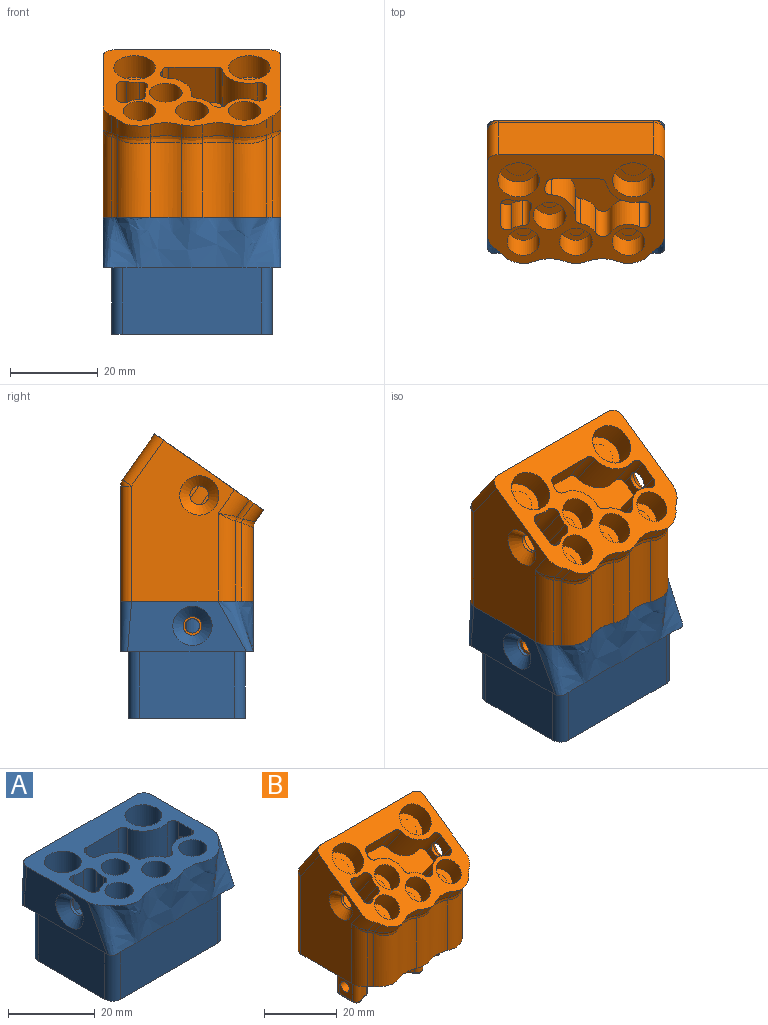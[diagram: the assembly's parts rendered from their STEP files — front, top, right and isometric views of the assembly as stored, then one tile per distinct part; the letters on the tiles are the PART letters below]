
ASSEMBLY  parts=2 mates=1
PART A: 55 faces, bbox 41.1x30.9x27.2 mm
  f0: cylinder r=1.6mm len=10mm, axis (0,0,1), area 29.4mm2, adj f1,f28,f29,f37,f47
  f1: plane 41.15x30.86mm, normal (0,0,1), area 665mm2, adj f0,f3,f4,f5,f6,f7,f8,f9
  f2: plane 40.88x30.59mm, normal (0,0,-1), area 253.7mm2, adj f3,f4,f5,f6,f7,f8,f38,f39
  f3: bspline ~40.6x11.6mm, area 535.9mm2, adj f1,f2,f4,f8
  f4: plane 27.1x11.6mm, normal (1,0,0), area 208.7mm2, adj f1,f2,f3,f5,f48
  f5: bspline ~39.24x28.84mm, area 37.4mm2, adj f1,f2,f4,f6
  f6: plane 37.4x11.6mm, normal (0,1,0), area 423.4mm2, adj f1,f2,f5,f7
  f7: bspline ~39.24x28.84mm, area 37.4mm2, adj f1,f2,f6,f8
  f8: plane 27.1x11.6mm, normal (-1,0,0), area 208.7mm2, adj f1,f2,f3,f7,f50
  f9: cylinder r=4.25mm len=26.7mm, axis (0,0,1), area 713mm2, adj f1,f46
  f10: cylinder r=3.25mm len=26.7mm, axis (0,0,1), area 545.2mm2, adj f1,f46
  f11: cylinder r=3.25mm len=26.7mm, axis (0,0,1), area 545.2mm2, adj f1,f46
  f12: cylinder r=4.25mm len=26.7mm, axis (0,0,1), area 713mm2, adj f1,f46
  f13: cylinder r=3.25mm len=26.7mm, axis (0,0,1), area 545.2mm2, adj f1,f46
  f14: cylinder r=3.25mm len=26.7mm, axis (0,0,1), area 545.2mm2, adj f1,f46
  f15: cylinder r=1.6mm len=10mm, axis (0,0,1), area 30.6mm2, adj f1,f16,f22,f23
  f16: plane 10x5.32mm, normal (1,0,0), area 38.7mm2, adj f1,f15,f17,f23,f49
  f17: cylinder r=1.6mm len=10mm, axis (0,0,1), area 35.3mm2, adj f1,f16,f18,f23
  f18: cylinder r=4.45mm len=10mm, axis (0,0,1), area 27mm2, adj f1,f17,f19,f23
  f19: cylinder r=1.6mm len=10mm, axis (0,0,1), area 27.7mm2, adj f1,f18,f20,f23
  f20: cylinder r=4.7mm len=10mm, axis (0,0,1), area 29.3mm2, adj f1,f19,f21,f23
  f21: cylinder r=1.6mm len=10mm, axis (0,0,1), area 35mm2, adj f1,f20,f22,f23
  f22: cylinder r=5.85mm len=10mm, axis (0,0,1), area 30.9mm2, adj f1,f15,f21,f23
  f23: plane 8.52x7.08mm, normal (0,0,1), area 49.5mm2, adj f15,f16,f17,f18,f19,f20,f21,f22
  f24: cylinder r=5.15mm len=10mm, axis (0,0,1), area 45.1mm2, adj f1,f25,f36,f37
  f25: cylinder r=1.85mm len=10mm, axis (0,0,1), area 39.4mm2, adj f1,f24,f26,f37
  f26: cylinder r=4.85mm len=10mm, axis (0,0,1), area 78.1mm2, adj f1,f25,f27,f37
  f27: cylinder r=1.6mm len=10mm, axis (0,0,1), area 34mm2, adj f1,f26,f28,f37
  f28: plane 10x4.21mm, normal (-1,0,0), area 28.1mm2, adj f0,f1,f27,f37,f47
  f29: cylinder r=6.25mm len=10mm, axis (0,0,1), area 106mm2, adj f0,f1,f30,f37
  f30: cylinder r=1.6mm len=10mm, axis (0,0,1), area 22.4mm2, adj f1,f29,f31,f37
  f31: plane 10.63x10mm, normal (0,-1,0), area 106.3mm2, adj f1,f30,f32,f37
  f32: cylinder r=1.6mm len=10mm, axis (0,0,1), area 22.4mm2, adj f1,f31,f33,f37
  f33: cylinder r=6.35mm len=10mm, axis (0,0,1), area 10.1mm2, adj f1,f32,f34,f37
  f34: cylinder r=1.6mm len=10mm, axis (0,0,1), area 29.5mm2, adj f1,f33,f35,f37
  f35: cylinder r=5.8mm len=10mm, axis (0,0,1), area 92.7mm2, adj f1,f34,f36,f37
  f36: cylinder r=1.6mm len=10mm, axis (0,0,1), area 23.2mm2, adj f1,f24,f35,f37
  f37: plane 24.18x16mm, normal (0,0,1), area 212.6mm2, adj f0,f24,f25,f26,f27,f28,f29,f30
  f38: plane 21.6x15.1mm, normal (1,0,0), area 317.6mm2, adj f2,f39,f45,f46,f54
  f39: cylinder r=2.5mm len=15.1mm, axis (0,0,1), area 59.3mm2, adj f2,f38,f40,f46
  f40: plane 31.6x15.1mm, normal (0,-1,0), area 477.2mm2, adj f2,f39,f41,f46
  f41: cylinder r=2.5mm len=15.1mm, axis (0,0,1), area 59.3mm2, adj f2,f40,f42,f46
  f42: plane 21.6x15.1mm, normal (-1,0,0), area 326.2mm2, adj f2,f41,f43,f46
  f43: cylinder r=2.5mm len=15.1mm, axis (0,0,1), area 59.3mm2, adj f2,f42,f44,f46
  f44: plane 31.6x15.1mm, normal (0,1,0), area 468.6mm2, adj f2,f43,f45,f46,f52
  f45: cylinder r=2.5mm len=15.1mm, axis (0,0,1), area 59.3mm2, adj f2,f38,f44,f46
  f46: plane 36.6x26.6mm, normal (0,0,-1), area 722mm2, adj f9,f10,f11,f12,f13,f14,f38,f39
  f47: cylinder r=2.15mm len=4.3mm, axis (1,0,0), area 13.1mm2, adj f0,f28,f48
  f48: cone r=2.15mm half-angle=45deg, axis (1,0,0), area 68.6mm2, adj f4,f47
  f49: cylinder r=2.15mm len=4.3mm, axis (-1,0,0), area 10.4mm2, adj f16,f50
  f50: cone r=2.15mm half-angle=45deg, axis (-1,0,0), area 68.6mm2, adj f8,f49
  f51: cone r=0mm half-angle=59deg, axis (0,1,0), area 10mm2, adj f52
  f52: cylinder r=1.65mm len=12.85mm, axis (0,1,0), area 133.2mm2, adj f44,f51
  f53: cone r=0mm half-angle=59deg, axis (1,0,0), area 10mm2, adj f54
  f54: cylinder r=1.65mm len=12.85mm, axis (1,0,0), area 133.2mm2, adj f38,f53
PART B: 167 faces, bbox 41.5x33.5x48.6 mm
  f0: torus R=0.85mm, axis (0,0,1), area 1.5mm2, adj f1,f164,f165,f166
  f1: cylinder r=1.45mm len=9mm, axis (0,0,1), area 25mm2, adj f0,f2,f162,f163
  f2: plane 40.6x30.3mm, normal (0,0,-1), area 534.2mm2, adj f1,f3,f8,f14,f20,f25,f31,f36
  f3: cylinder r=4mm len=8mm, axis (0,0,-1), area 175.9mm2, adj f2,f4
  f4: plane 8x8mm, normal (0,0,-1), area 37.7mm2, adj f3,f5
  f5: cylinder r=2mm len=15.32mm, axis (0,0,1), area 184.6mm2, adj f4,f6
  f6: cylinder r=2mm len=4.78mm, axis (0,-0.57,0.82), area 25mm2, adj f5,f7
  f7: plane 4x3.28mm, normal (0,0.57,-0.82), area 12.6mm2, adj f6
  f8: cylinder r=4mm len=8mm, axis (0,0,-1), area 175.9mm2, adj f2,f9
  f9: plane 8x8mm, normal (0,0,-1), area 37.7mm2, adj f8,f10
  f10: cylinder r=2mm len=12.7mm, axis (0,0,1), area 149.9mm2, adj f9,f11,f12,f13
  f11: cylinder r=2mm len=3.54mm, axis (0,-0.57,0.82), area 0mm2, adj f10,f13
  f12: cylinder r=2.55mm len=1.79mm, axis (0,-0.57,0.82), area 0mm2, adj f10,f13
  f13: plane 4.88x4.61mm, normal (0,0.57,-0.82), area 14.6mm2, adj f10,f11,f12
  f14: cylinder r=4mm len=8mm, axis (0,0,-1), area 175.9mm2, adj f2,f15
  f15: plane 8x8mm, normal (0,0,-1), area 37.7mm2, adj f14,f16
  f16: cylinder r=2mm len=12.7mm, axis (0,0,1), area 149.9mm2, adj f15,f17,f18,f19
  f17: cylinder r=2mm len=3.54mm, axis (0,-0.57,0.82), area 0mm2, adj f16,f19
  f18: cylinder r=2.55mm len=1.79mm, axis (0,-0.57,0.82), area 0mm2, adj f16,f19
  f19: plane 4.88x4.61mm, normal (0,0.57,-0.82), area 14.6mm2, adj f16,f17,f18
  f20: cylinder r=5.5mm len=11mm, axis (0,0,-1), area 241.9mm2, adj f2,f21
  f21: plane 11x11mm, normal (0,0,-1), area 66.8mm2, adj f20,f22
  f22: cylinder r=3mm len=18.78mm, axis (0,0,1), area 336.1mm2, adj f21,f23
  f23: cylinder r=3mm len=8.42mm, axis (0,-0.57,0.82), area 96.7mm2, adj f22,f24
  f24: plane 6x4.92mm, normal (0,0.57,-0.82), area 28.3mm2, adj f23
  f25: cylinder r=4mm len=8mm, axis (0,0,-1), area 175.9mm2, adj f2,f26
  f26: plane 8x8mm, normal (0,0,-1), area 37.7mm2, adj f25,f27
  f27: cylinder r=2mm len=12.7mm, axis (0,0,1), area 149.9mm2, adj f26,f28,f29,f30
  f28: cylinder r=2mm len=3.54mm, axis (0,-0.57,0.82), area 0mm2, adj f27,f30
  f29: cylinder r=2.55mm len=1.79mm, axis (0,-0.57,0.82), area 0mm2, adj f27,f30
  f30: plane 4.88x4.61mm, normal (0,0.57,-0.82), area 14.6mm2, adj f27,f28,f29
  f31: cylinder r=5.5mm len=11mm, axis (0,0,-1), area 241.9mm2, adj f2,f32
  f32: plane 11x11mm, normal (0,0,-1), area 66.8mm2, adj f31,f33
  f33: cylinder r=3mm len=18.78mm, axis (0,0,1), area 336.1mm2, adj f32,f34
  f34: cylinder r=3mm len=8.42mm, axis (0,-0.57,0.82), area 96.7mm2, adj f33,f35
  f35: plane 6x4.92mm, normal (0,0.57,-0.82), area 28.3mm2, adj f34
  f36: plane 36.72x23.51mm, normal (1,0,0), area 585.1mm2, adj f2,f37,f55,f100,f101,f102,f114
  f37: cylinder r=5mm len=7.66mm, axis (0,-0.57,0.82), area 26.1mm2, adj f36,f38,f54,f55
  f38: bspline ~4.63x2.45mm, area 2.1mm2, adj f37,f39,f114
  f39: bspline ~2.24x1.89mm, area 1.8mm2, adj f38,f40,f54,f113
  f40: bspline ~8.46x3.82mm, area 11.6mm2, adj f39,f41,f53,f112
  f41: cylinder r=6.05mm len=7.57mm, axis (0,-0.57,0.82), area 33.8mm2, adj f40,f42,f54,f55
  f42: cylinder r=8.45mm len=6.99mm, axis (0,-0.57,0.82), area 24.9mm2, adj f41,f43,f53,f55
  f43: cylinder r=6.05mm len=5.01mm, axis (0,-0.57,0.82), area 17.8mm2, adj f42,f44,f52,f55
  f44: bspline ~6.05x1.6mm, area 7.6mm2, adj f43,f45,f53,f110
  f45: bspline ~8.63x1.68mm, area 10.8mm2, adj f44,f46,f52,f109
  f46: bspline ~8.46x3.82mm, area 11.6mm2, adj f45,f47,f51,f108
  f47: cylinder r=6.05mm len=7.57mm, axis (0,-0.57,0.82), area 33.8mm2, adj f46,f48,f52,f55
  f48: cylinder r=5mm len=4.53mm, axis (0,-0.57,0.82), area 8mm2, adj f47,f49,f51,f55
  f49: cylinder r=5mm len=7.66mm, axis (0,-0.57,0.82), area 26.1mm2, adj f48,f50,f55,f105
  f50: bspline ~4.63x2.45mm, area 3.2mm2, adj f49,f51,f106
  f51: bspline ~2.24x1.89mm, area 1.8mm2, adj f46,f48,f50,f107
  f52: cylinder r=8.45mm len=6.99mm, axis (0,-0.57,0.82), area 24.9mm2, adj f43,f45,f47,f55
  f53: bspline ~8.63x1.68mm, area 10.8mm2, adj f40,f42,f44,f111
  f54: cylinder r=5mm len=4.53mm, axis (0,-0.57,0.82), area 8mm2, adj f37,f39,f41,f55
  f55: plane 40.6x24.82mm, normal (0,-0.57,0.82), area 592.7mm2, adj f36,f37,f41,f42,f43,f47,f48,f49
  f56: cylinder r=4.85mm len=9.6mm, axis (0,-0.57,0.82), area 78.1mm2, adj f55,f57,f58,f71
  f57: plane 24.18x13.11mm, normal (0,-0.57,0.82), area 212.6mm2, adj f56,f58,f59,f61,f62,f63,f64,f65
  f58: cylinder r=1.6mm len=9.11mm, axis (0,-0.57,0.82), area 34mm2, adj f55,f56,f57,f59
  f59: plane 10.61x9.19mm, normal (-1,0,0), area 28.1mm2, adj f55,f57,f58,f60,f61
  f60: cylinder r=2.15mm len=4.3mm, axis (1,0,0), area 13.1mm2, adj f59,f61,f101
  f61: cylinder r=1.6mm len=9.11mm, axis (0,-0.57,0.82), area 29.4mm2, adj f55,f57,f59,f60,f62
  f62: cylinder r=6.25mm len=11.16mm, axis (0,-0.57,0.82), area 106mm2, adj f55,f57,f61,f63
  f63: cylinder r=1.6mm len=8.95mm, axis (0,-0.57,0.82), area 22.4mm2, adj f55,f57,f62,f64
  f64: plane 10.63x8.19mm, normal (0,-0.82,-0.57), area 106.3mm2, adj f55,f57,f63,f65
  f65: cylinder r=1.6mm len=8.95mm, axis (0,-0.57,0.82), area 22.4mm2, adj f55,f57,f64,f66
  f66: cylinder r=6.35mm len=8.75mm, axis (0,-0.57,0.82), area 10.1mm2, adj f55,f57,f65,f67
  f67: cylinder r=1.6mm len=9.41mm, axis (0,-0.57,0.82), area 29.5mm2, adj f55,f57,f66,f68
  f68: cylinder r=5.8mm len=11.8mm, axis (0,-0.57,0.82), area 92.7mm2, adj f55,f57,f67,f69
  f69: cylinder r=1.6mm len=9.17mm, axis (0,-0.57,0.82), area 23.2mm2, adj f55,f57,f68,f70
  f70: cylinder r=5.15mm len=9.69mm, axis (0,-0.57,0.82), area 45.1mm2, adj f55,f57,f69,f71
  f71: cylinder r=1.85mm len=8.75mm, axis (0,-0.57,0.82), area 39.4mm2, adj f55,f56,f57,f70
  f72: cylinder r=2.5mm len=11.89mm, axis (0,-0.57,0.82), area 50.1mm2, adj f55,f73,f76,f105
  f73: sphere r=2.5mm, area 2.9mm2, adj f72,f74,f104
  f74: cylinder r=2.5mm len=35.6mm, axis (1,0,0), area 54.4mm2, adj f73,f75,f76,f103
  f75: sphere r=2.5mm, area 2.9mm2, adj f74,f100,f102
  f76: plane 35.6x10.46mm, normal (0,0.82,0.57), area 454.4mm2, adj f55,f72,f74,f100
  f77: cylinder r=4.75mm len=11.22mm, axis (0,-0.57,0.82), area 179.1mm2, adj f55,f78
  f78: plane 9.5x7.78mm, normal (0,-0.57,0.82), area 70.9mm2, adj f77
  f79: cylinder r=3.75mm len=9.59mm, axis (0,-0.57,0.82), area 141.4mm2, adj f55,f80
  f80: plane 7.5x6.14mm, normal (0,-0.57,0.82), area 44.2mm2, adj f79
  f81: cylinder r=3.75mm len=9.59mm, axis (0,-0.57,0.82), area 141.4mm2, adj f55,f82
  f82: plane 7.5x6.14mm, normal (0,-0.57,0.82), area 44.2mm2, adj f81
  f83: cylinder r=3.75mm len=9.59mm, axis (0,-0.57,0.82), area 141.4mm2, adj f55,f84
  f84: plane 7.5x6.14mm, normal (0,-0.57,0.82), area 44.2mm2, adj f83
  f85: cylinder r=3.75mm len=9.59mm, axis (0,-0.57,0.82), area 141.4mm2, adj f55,f86
  f86: plane 7.5x6.14mm, normal (0,-0.57,0.82), area 44.2mm2, adj f85
  f87: cylinder r=4.75mm len=11.22mm, axis (0,-0.57,0.82), area 179.1mm2, adj f55,f88
  f88: plane 9.5x7.78mm, normal (0,-0.57,0.82), area 70.9mm2, adj f87
  f89: plane 11.24x10.09mm, normal (1,0,0), area 38.7mm2, adj f55,f90,f91,f93,f99
  f90: plane 7.08x6.98mm, normal (0,-0.57,0.82), area 49.5mm2, adj f89,f93,f94,f95,f96,f97,f98,f99
  f91: cylinder r=2.15mm len=4.3mm, axis (-1,0,0), area 10.4mm2, adj f89,f92
  f92: cone r=2.15mm half-angle=45deg, axis (-1,0,0), area 68.6mm2, adj f91,f105
  f93: cylinder r=1.6mm len=9.11mm, axis (0,-0.57,0.82), area 35.3mm2, adj f55,f89,f90,f94
  f94: cylinder r=4.45mm len=8.69mm, axis (0,-0.57,0.82), area 27mm2, adj f55,f90,f93,f95
  f95: cylinder r=1.6mm len=9.28mm, axis (0,-0.57,0.82), area 27.7mm2, adj f55,f90,f94,f96
  f96: cylinder r=4.7mm len=9.83mm, axis (0,-0.57,0.82), area 29.3mm2, adj f55,f90,f95,f97
  f97: cylinder r=1.6mm len=9.49mm, axis (0,-0.57,0.82), area 35mm2, adj f55,f90,f96,f98
  f98: cylinder r=5.85mm len=8.39mm, axis (0,-0.57,0.82), area 30.9mm2, adj f55,f90,f97,f99
  f99: cylinder r=1.6mm len=9.11mm, axis (0,-0.57,0.82), area 30.6mm2, adj f55,f89,f90,f98
  f100: cylinder r=2.5mm len=11.89mm, axis (0,-0.57,0.82), area 50.1mm2, adj f36,f55,f75,f76
  f101: cone r=2.15mm half-angle=45deg, axis (1,0,0), area 68.6mm2, adj f36,f60
  f102: cylinder r=2.5mm len=26.27mm, axis (0,0,1), area 103.1mm2, adj f2,f36,f75,f103
  f103: plane 35.6x26.27mm, normal (0,1,0), area 935mm2, adj f2,f74,f102,f104
  f104: cylinder r=2.5mm len=26.27mm, axis (0,0,1), area 103.1mm2, adj f2,f73,f103,f105
  f105: plane 36.72x23.51mm, normal (-1,0,0), area 585.1mm2, adj f2,f49,f55,f72,f92,f104,f106
  f106: cylinder r=5mm len=20.04mm, axis (0,0,1), area 89.1mm2, adj f2,f50,f105,f107
  f107: cylinder r=5mm len=18.13mm, axis (0,0,1), area 32mm2, adj f2,f51,f106,f108
  f108: cylinder r=6.05mm len=17.93mm, axis (0,0,1), area 149.7mm2, adj f2,f46,f107,f109
  f109: cylinder r=8.45mm len=16.95mm, axis (0,0,1), area 122.2mm2, adj f2,f45,f108,f110
  f110: cylinder r=6.05mm len=16.95mm, axis (0,0,1), area 87.5mm2, adj f2,f44,f109,f111
  f111: cylinder r=8.45mm len=16.95mm, axis (0,0,1), area 122.2mm2, adj f2,f53,f110,f112
  f112: cylinder r=6.05mm len=17.93mm, axis (0,0,1), area 149.7mm2, adj f2,f40,f111,f113
  f113: cylinder r=5mm len=18.13mm, axis (0,0,1), area 32mm2, adj f2,f39,f112,f114
  f114: cylinder r=5mm len=20.04mm, axis (0,0,1), area 89.1mm2, adj f2,f36,f38,f113
  f115: cylinder r=1.45mm len=9mm, axis (0,0,1), area 28.4mm2, adj f2,f116,f121,f126,f127,f163
  f116: bspline ~1.53x0.23mm, area 0.2mm2, adj f115,f117,f119,f120
  f117: bspline ~3.01x1.09mm, area 0.4mm2, adj f116,f118,f119,f126
  f118: bspline ~1.14x0.12mm, area 0.1mm2, adj f117,f119,f120,f128
  f119: cylinder r=1.65mm len=6.56mm, axis (-1,0,0), area 65.7mm2, adj f116,f117,f118,f120,f162
  f120: bspline ~3.01x1.08mm, area 0.4mm2, adj f116,f118,f119,f127
  f121: torus R=0.85mm, axis (0,0,1), area 1.8mm2, adj f115,f122,f165,f166
  f122: torus R=5.45mm, axis (0,0,1), area 1.8mm2, adj f121,f123,f126,f165
  f123: torus R=0.85mm, axis (0,0,1), area 1.4mm2, adj f122,f124,f128,f165
  f124: torus R=5.2mm, axis (0,0,1), area 1.7mm2, adj f123,f125,f129,f165
  f125: torus R=0.85mm, axis (0,0,1), area 1.8mm2, adj f124,f130,f164,f165
  f126: cylinder r=4.85mm len=2.95mm, axis (0,0,1), area 8.1mm2, adj f115,f117,f122,f128
  f127: cylinder r=4.85mm len=5.08mm, axis (0,0,1), area 15.1mm2, adj f2,f115,f120,f128
  f128: cylinder r=1.45mm len=9mm, axis (0,0,1), area 22.5mm2, adj f2,f118,f123,f126,f127,f129
  f129: cylinder r=4.6mm len=9mm, axis (0,0,1), area 25.1mm2, adj f2,f124,f128,f130
  f130: cylinder r=1.45mm len=9mm, axis (0,0,1), area 28.8mm2, adj f2,f125,f129,f162
  f131: cylinder r=1.45mm len=9mm, axis (0,0,1), area 18.3mm2, adj f2,f132,f147,f161
  f132: torus R=0.85mm, axis (0,0,1), area 1.1mm2, adj f131,f133,f145,f146
  f133: torus R=7.1mm, axis (0,0,1), area 0.6mm2, adj f132,f134,f145,f161
  f134: torus R=0.85mm, axis (0,0,1), area 1.5mm2, adj f133,f135,f145,f160
  f135: torus R=6.55mm, axis (0,0,1), area 5.7mm2, adj f134,f136,f145,f159
  f136: torus R=0.85mm, axis (0,0,1), area 1.2mm2, adj f135,f137,f145,f158
  f137: torus R=5.9mm, axis (0,0,1), area 2.8mm2, adj f136,f138,f145,f157
  f138: torus R=1.1mm, axis (0,0,1), area 2mm2, adj f137,f139,f145,f156
  f139: torus R=5.6mm, axis (0,0,1), area 4.9mm2, adj f138,f140,f145,f155
  f140: torus R=0.85mm, axis (0,0,1), area 1.7mm2, adj f139,f141,f145,f154
  f141: cylinder r=0.6mm len=4.21mm, axis (0,-1,0), area 2.5mm2, adj f140,f142,f145,f151
  f142: torus R=0.85mm, axis (0,0,1), area 1.5mm2, adj f141,f143,f145,f150
  f143: torus R=7mm, axis (0,0,1), area 6.5mm2, adj f142,f144,f145,f149
  f144: torus R=0.85mm, axis (0,0,1), area 1.1mm2, adj f143,f145,f146,f148
  f145: plane 23.34x15.16mm, normal (0,0,-1), area 184.6mm2, adj f132,f133,f134,f135,f136,f137,f138,f139
  f146: cylinder r=0.6mm len=10.63mm, axis (1,0,0), area 6.3mm2, adj f132,f144,f145,f147
  f147: plane 10.63x9mm, normal (0,1,0), area 95.7mm2, adj f2,f131,f146,f148
  f148: cylinder r=1.45mm len=9mm, axis (0,0,1), area 18.2mm2, adj f2,f144,f147,f149
  f149: cylinder r=6.4mm len=9mm, axis (0,0,1), area 97.7mm2, adj f2,f143,f148,f150
  f150: cylinder r=1.45mm len=9mm, axis (0,0,1), area 24.4mm2, adj f2,f142,f149,f151
  f151: plane 9x4.21mm, normal (1,0,0), area 29.4mm2, adj f2,f141,f150,f152,f154
  f152: cylinder r=1.65mm len=10.1mm, axis (1,0,0), area 104.7mm2, adj f151,f153
  f153: cone r=0mm half-angle=59deg, axis (1,0,0), area 10mm2, adj f152
  f154: cylinder r=1.45mm len=9mm, axis (0,0,1), area 27.7mm2, adj f2,f140,f151,f155
  f155: cylinder r=5mm len=9mm, axis (0,0,1), area 72.5mm2, adj f2,f139,f154,f156
  f156: cylinder r=1.7mm len=9mm, axis (0,0,1), area 32.6mm2, adj f2,f138,f155,f157
  f157: cylinder r=5.3mm len=9mm, axis (0,0,1), area 41.8mm2, adj f2,f137,f156,f158
  f158: cylinder r=1.45mm len=9mm, axis (0,0,1), area 18.9mm2, adj f2,f136,f157,f159
  f159: cylinder r=5.95mm len=9mm, axis (0,0,1), area 85.6mm2, adj f2,f135,f158,f160
  f160: cylinder r=1.45mm len=9mm, axis (0,0,1), area 24.1mm2, adj f2,f134,f159,f161
  f161: cylinder r=6.5mm len=9mm, axis (0,0,1), area 9.3mm2, adj f2,f131,f133,f160
  f162: plane 9x5.32mm, normal (-1,0,0), area 39.3mm2, adj f1,f2,f119,f130,f164
  f163: cylinder r=6mm len=9mm, axis (0,0,1), area 28.5mm2, adj f1,f2,f115,f166
  f164: cylinder r=0.6mm len=5.32mm, axis (0,1,0), area 3.1mm2, adj f0,f125,f162,f165
  f165: plane 7.68x6.24mm, normal (0,0,-1), area 38.8mm2, adj f0,f121,f122,f123,f124,f125,f164,f166
  f166: torus R=6.6mm, axis (0,0,1), area 1.9mm2, adj f0,f121,f163,f165
PLACE A at identity
PLACE B t=(0,0,11.6)mm
MATE fastened B.f8 <-> A.f10  axis (0,0,-1) through (20.3,6.05,11.6)mm
